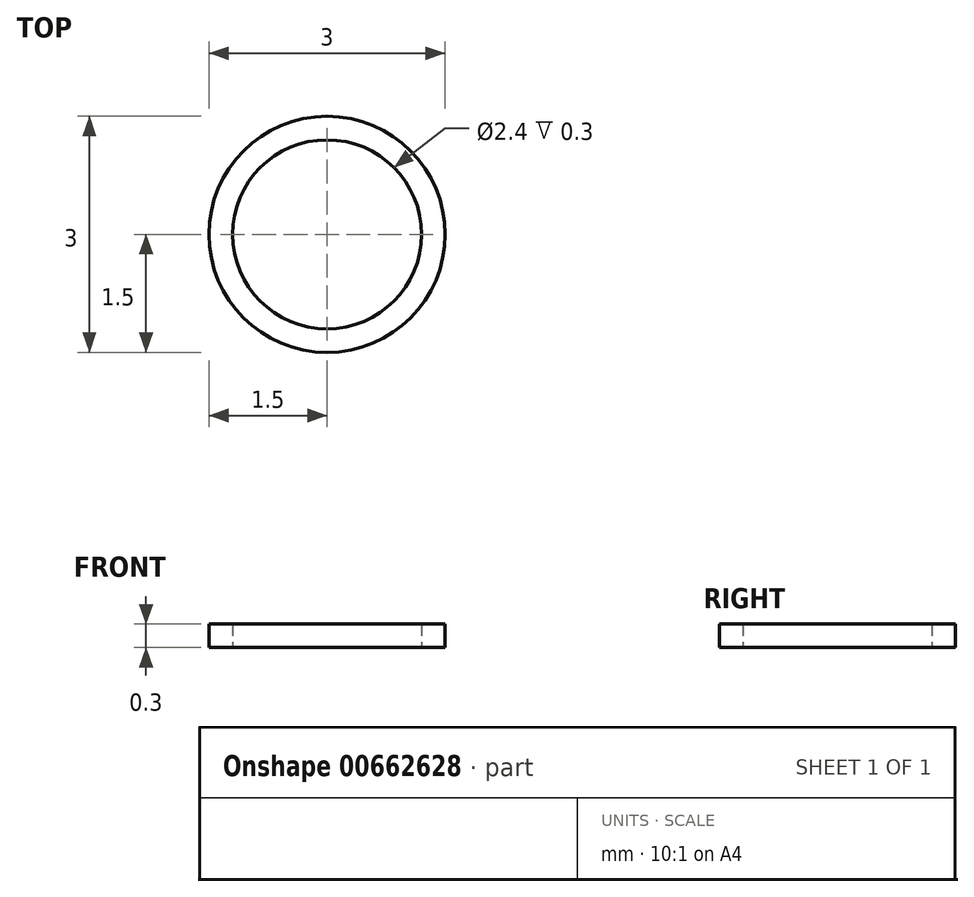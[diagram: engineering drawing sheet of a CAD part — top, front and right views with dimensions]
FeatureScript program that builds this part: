
annotation { "Feature Type Name" : "Feature", "Feature Type Description" : "" }
export const myFeature = defineFeature(function(context is Context, id is Id, definition is map)
    precondition{}
    {
        {
            var Q0;
            Q0=qCreatedBy(makeId("Top.planeOp"),FACE);
            var sketch = newSketch(context, id + "F0", { "sketchPlane" : qUnion([Q0])});
            skCircle(sketch, "E0", {"center": v(0, 0) * mm, "radius": 1.2 * mm});
            skCircle(sketch, "E1.0", {"center": v(0, 0) * mm, "radius": 1.5 * mm});
            skSolve(sketch);
        }
        {
            var Q0;
            Q0=makeQuery(id+"F0.imprint","IMPRINT",FACE,{"disambiguationData":[TD([[makeQuery(id+"F0.imprint","IMPRINT",EDGE,{"derivedFrom":sQuery(id+"F0.wireOp",EDGE,"E0")}),-1.0]])]});
            extrude(context, id + "F1", {"entities" : qUnion([Q0]), "depth" : .3 * mm, "offsetDistance" : 25 * mm});
        }
    });
